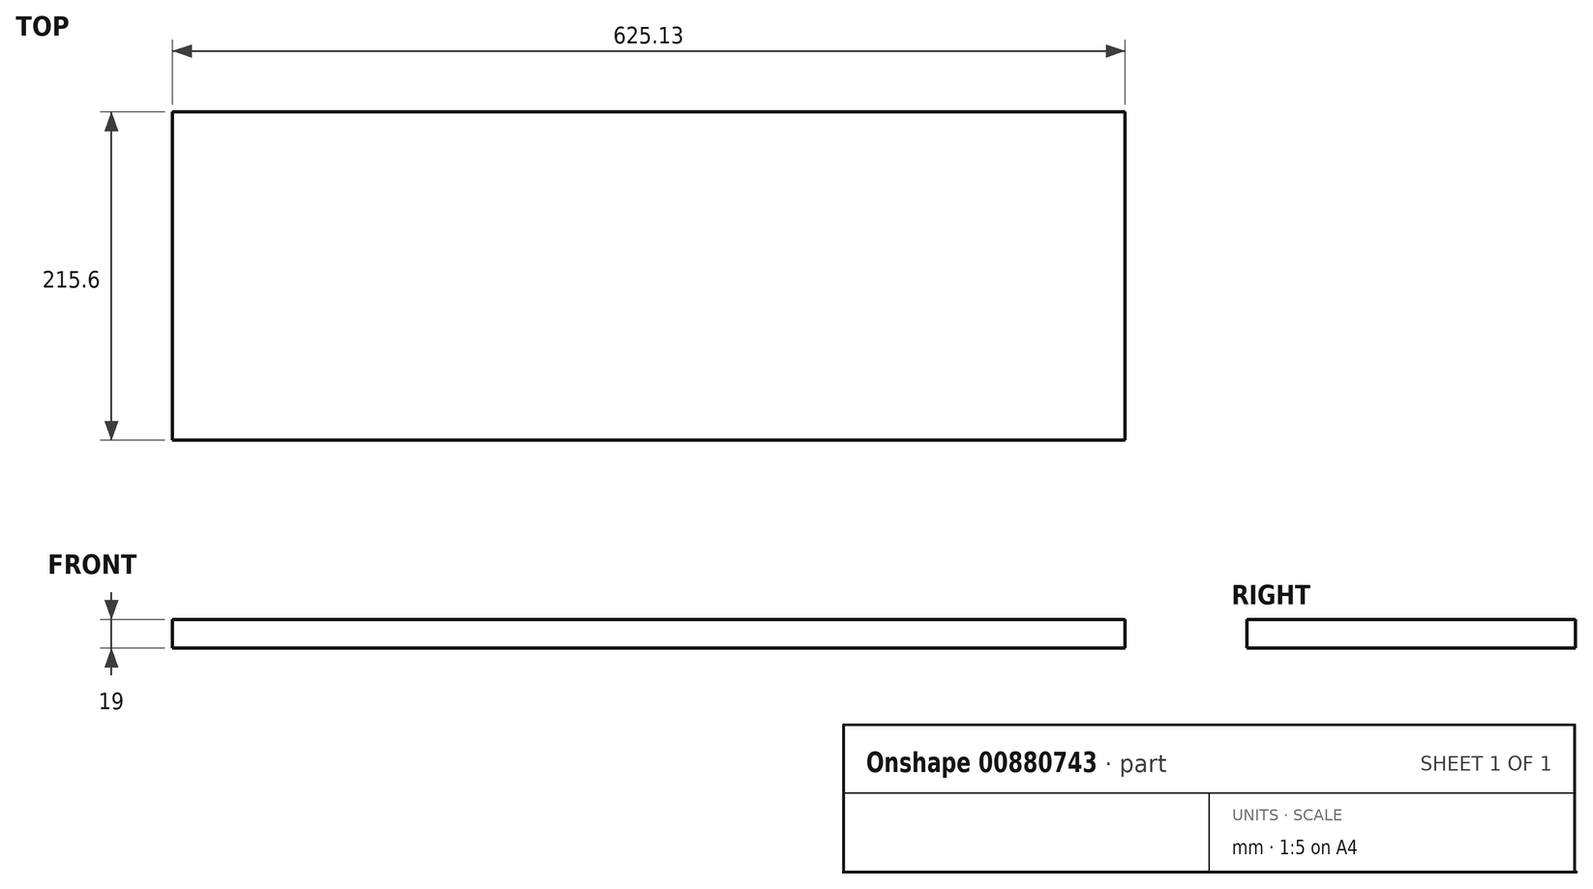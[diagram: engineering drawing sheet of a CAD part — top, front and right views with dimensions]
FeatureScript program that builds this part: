
annotation { "Feature Type Name" : "Feature", "Feature Type Description" : "" }
export const myFeature = defineFeature(function(context is Context, id is Id, definition is map)
    precondition{}
    {
        {
            var Q0;
            Q0=qCreatedBy(makeId("Top.planeOp"),FACE);
            var sketch = newSketch(context, id + "F0", { "sketchPlane" : qUnion([Q0])});
            skPoint(sketch, "E0.0", {"position": v(0, 0) * mm});
            skLineSegment(sketch, "E1.bottom", {"start": v(0, 0) * mm, "end": v(75.13, 0) * mm});
            skLineSegment(sketch, "E1.top", {"start": v(0, -75.6) * mm, "end": v(75.13, -75.6) * mm});
            skLineSegment(sketch, "E1.left", {"start": v(0, 0) * mm, "end": v(0, -75.6) * mm});
            skLineSegment(sketch, "E1.right", {"start": v(75.13, 0) * mm, "end": v(75.13, -75.6) * mm});
            skSolve(sketch);
        }
        {
            var Q0;
            Q0 = qSketchRegion(id + "F0", true);
            extrude(context, id + "F1", {"entities" : qUnion([Q0]), "surfaceOperationType" : NewSurfaceOperationType.ADD, "depth" : 19 * mm, "offsetDistance" : 25 * mm});
        }
        {
            var Q0;
            Q0=makeQuery(id+"F1.opExtrude","SWEPT_FACE",FACE,{"disambiguationData":[OSD([sQuery(id+"F0.wireOp",EDGE,"E1.right")])]});
            extrude(context, id + "F2", {"entities" : qUnion([Q0]), "operationType" : NewBodyOperationType.ADD, "depth" : 50 * mm, "offsetDistance" : 25 * mm});
        }
        {
            var Q0;
            Q0=makeQuery(id+"F2.opExtrude","CAP_FACE",FACE,{"disambiguationData":[OSD([sQuery(id+"F0.wireOp",EDGE,"E1.right")])],"isStart":false});
            extrude(context, id + "F3", {"entities" : qUnion([Q0]), "operationType" : NewBodyOperationType.ADD, "depth" : 500 * mm, "offsetDistance" : 25 * mm});
        }
        {
            var Q0;
            {var subQ0=sQuery(id+"F0.wireOp",EDGE,"E1.right");var subQ1=sQuery(id+"F0.wireOp",EDGE,"E1.top");Q0=makeQuery(id+"F3.boolean.opBoolean","MERGE",FACE,{"derivedFrom":[makeQuery(id+"F2.boolean.opBoolean","MERGE",FACE,{"derivedFrom":[makeQuery(id+"F1.opExtrude","SWEPT_FACE",FACE,{"disambiguationData":[OSD([subQ1])]}),makeQuery(id+"F2.opExtrude","SWEPT_FACE",FACE,{"disambiguationData":[OSD([subQ1,subQ0])]})]}),makeQuery(id+"F3.opExtrude","SWEPT_FACE",FACE,{"disambiguationData":[OSD([subQ1,subQ0])]})]});}
            extrude(context, id + "F4", {"entities" : qUnion([Q0]), "operationType" : NewBodyOperationType.ADD, "depth" : 140 * mm, "offsetDistance" : 25 * mm});
        }
    });
